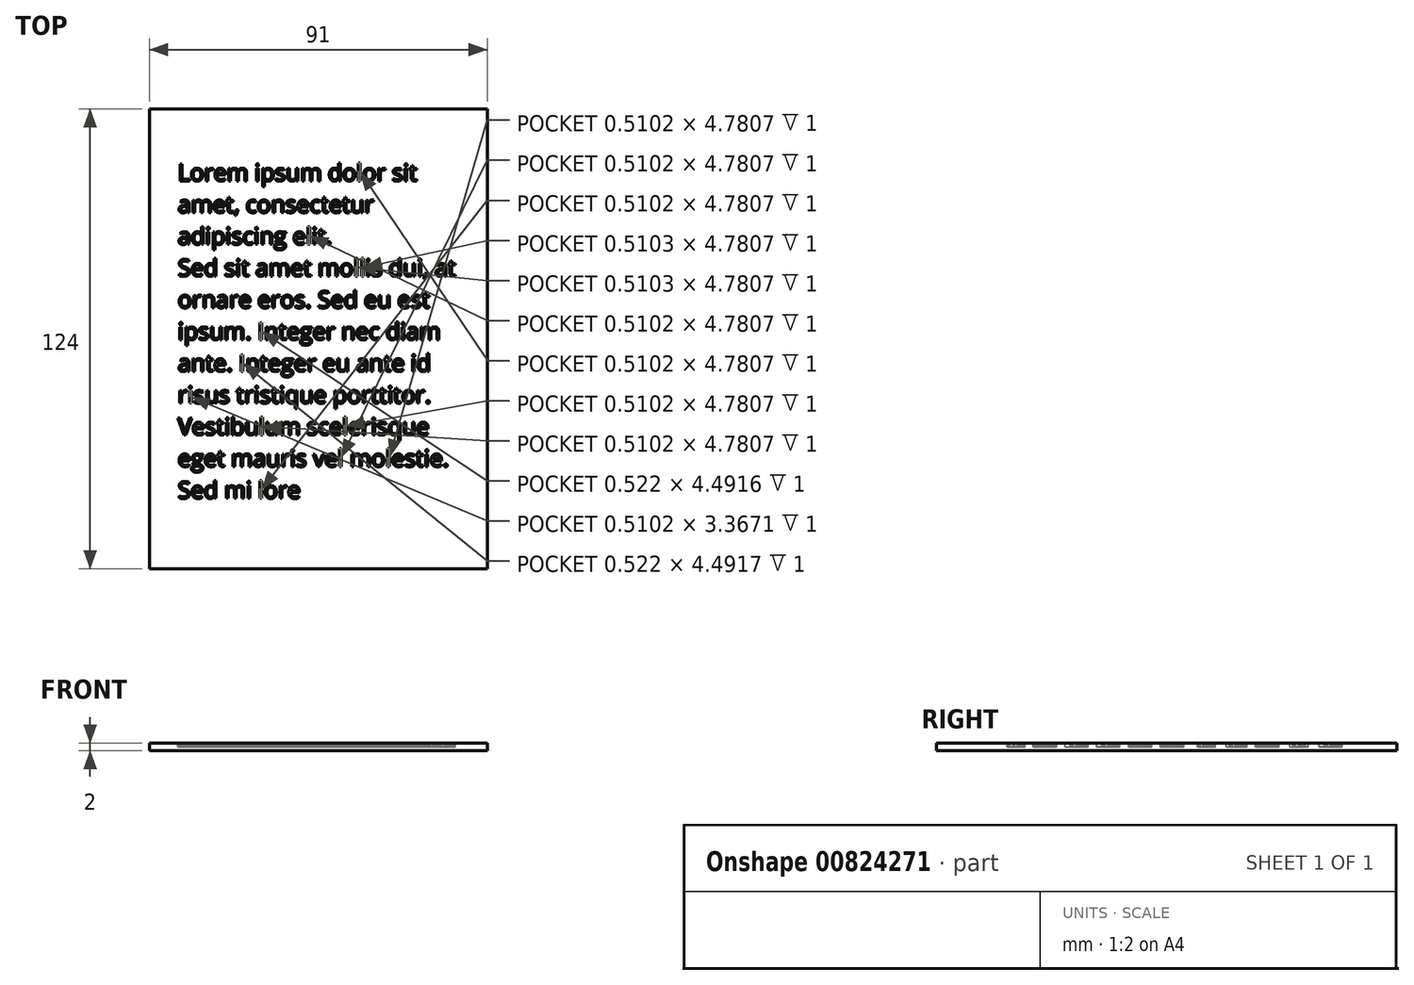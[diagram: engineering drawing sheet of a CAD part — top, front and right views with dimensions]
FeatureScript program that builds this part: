
annotation { "Feature Type Name" : "Feature", "Feature Type Description" : "" }
export const myFeature = defineFeature(function(context is Context, id is Id, definition is map)
    precondition{}
    {
        {
            var Q0;
            Q0=qCreatedBy(makeId("Top.planeOp"),FACE);
            var sketch = newSketch(context, id + "F0", { "sketchPlane" : qUnion([Q0])});
            skLineSegment(sketch, "E0.bottom", {"start": v(-64.49, 87.53) * mm, "end": v(26.51, 87.53) * mm});
            skLineSegment(sketch, "E0.top", {"start": v(-64.49, -36.47) * mm, "end": v(26.51, -36.47) * mm});
            skLineSegment(sketch, "E0.left", {"start": v(-64.49, 87.53) * mm, "end": v(-64.49, -36.47) * mm});
            skLineSegment(sketch, "E0.right", {"start": v(26.51, 87.53) * mm, "end": v(26.51, -36.47) * mm});
            skSolve(sketch);
        }
        {
            var Q0;
            Q0=makeQuery(id+"F0.imprint","IMPRINT",FACE,{"disambiguationData":[TD([[makeQuery(id+"F0.imprint","IMPRINT",EDGE,{"derivedFrom":sQuery(id+"F0.wireOp",EDGE,"E0.bottom")}),-1.0]])]});
            extrude(context, id + "F1", {"entities" : qUnion([Q0]), "depth" : 2 * mm, "offsetDistance" : 25 * mm});
        }
        {
            var Q0;
            Q0=makeQuery(id+"F1.opExtrude","CAP_FACE",FACE,{"disambiguationData":[OSD([sQuery(id+"F0.wireOp",EDGE,"E0.bottom"),sQuery(id+"F0.wireOp",EDGE,"E0.top"),sQuery(id+"F0.wireOp",EDGE,"E0.left"),sQuery(id+"F0.wireOp",EDGE,"E0.right")])],"isStart":false});
            var sketch = newSketch(context, id + "F2", { "sketchPlane" : qUnion([Q0])});
            skText(sketch, "E1", { "text": "Lorem ipsum dolor sit\namet, consectetur \nadipiscing elit.\nSed sit amet mollis dui, at \nornare eros. Sed eu est\nipsum. Integer nec diam\nante. Integer eu ante id\nrisus tristique porttitor. \nVestibulum scelerisque \neget mauris vel molestie. \nSed mi lore", "fontName": "OpenSans-Regular.ttf"});
            const initialGuessF2  = {"E1": [-0.05686, 0.06811, 1, 0, 0.00453]};
            skSetInitialGuess(sketch, initialGuessF2);
            skSolve(sketch);
        }
        {
            var Q0;
            Q0=qSketchRegion(id+"F2",true);
            extrude(context, id + "F3", {"entities" : qUnion([Q0]), "operationType" : NewBodyOperationType.REMOVE, "oppositeDirection" : true, "depth" : 1 * mm, "offsetDistance" : 25 * mm});
        }
    });
